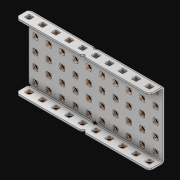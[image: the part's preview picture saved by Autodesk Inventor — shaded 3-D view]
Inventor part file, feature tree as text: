
AUTODESK INVENTOR PART (.ipt)
format: ipt  version: 2021 (Build 250183000, 183)  size: 3,073,024 bytes
history: native  units: in
note: dims shown in document units (in); Inventor stores cm internally (conversion verified against a paired STEP export)
features: extrude x71, other x70, sketch x4, thicken_offset x3, pattern_linear x3, imported_body x1
ambient origin geometry x8: Origin, YZ Plane, XZ Plane, XY Plane, X Axis, Y Axis, Z Axis, Center Point
bodies: Solid1 (feature_tree)
feature tree (152):
  thicken_offset  "Thicken1"
  thicken_offset  "Thicken2"
  thicken_offset  "Thicken3"
  pattern_linear  "Rectangular Pattern1"  Spacing1=0.001in  [1 undecoded]
  pattern_linear  "Rectangular Pattern2"  Spacing1=0.001in  [1 undecoded]
  pattern_linear  "Rectangular Pattern3"  Spacing1=0.182in  [1 undecoded]
  extrude  "Extrusion1"  Depth=0.063in TaperAngle=0.0deg
  sketch  "Sketch1"  dims[d0=0.001in]
  other  "Srf1"
  sketch  "Sketch2"  dims[d1=0.001in]
  other  "Srf2"
  sketch  "Sketch3"  dims[d2=0.001in]
  other  "Srf3"
  other  "Srf4"
  other  "Srf5"
  other  "Srf6"
  other  "Srf7"
  other  "Srf8"
  other  "Srf9"
  other  "Srf10"
  other  "Srf11"
  other  "Srf12"
  other  "Srf38"
  other  "Srf39"
  other  "Srf40"
  other  "Srf41"
  other  "Srf42"
  other  "Srf43"
  other  "Srf44"
  other  "Srf45"
  other  "Srf46"
  other  "Srf72"
  other  "Srf73"
  other  "Srf74"
  other  "Srf75"
  other  "Srf76"
  other  "Srf77"
  other  "Srf78"
  other  "Srf79"
  other  "Srf80"
  other  "Srf106"
  other  "Srf107"
  other  "Srf108"
  other  "Srf109"
  other  "Srf110"
  other  "Srf111"
  other  "Srf112"
  other  "Srf113"
  other  "Srf114"
  other  "Srf115"
  other  "Srf141"
  other  "Srf142"
  other  "Srf143"
  other  "Srf144"
  other  "Srf145"
  other  "Srf146"
  other  "Srf147"
  other  "Srf148"
  other  "Srf149"
  other  "Srf150"
  other  "Srf176"
  other  "Srf177"
  other  "Srf178"
  other  "Srf179"
  other  "Srf180"
  other  "Srf181"
  other  "Srf182"
  other  "Srf183"
  other  "Srf184"
  other  "Srf185"
  other  "Srf211"
  other  "Srf212"
  other  "Srf213"
  other  "Srf214"
  other  "Srf215"
  other  "Srf216"
  other  "Srf217"
  other  "Srf218"
  other  "Srf219"
  other  "Srf220"
  sketch  "Sketch4"  dims[d3=0.001in d4=0.001in d5=0.001in d6=0.182in d7=0.063in d8=0.0in d9=0.182in d10=0.063in d11=0.0in d12=0.182in d13=0.063in d14=0.0in d17=0.5in d18=3.937in d20=0.5in d21=3.937in d23=0.5in d24=1.9685in d26=0.5in d27=12.5in d28=0.0in]
  imported_body  "Imported1"
  extrude  "ExtrusionSrf1"  Depth=0.063in
  extrude  "ExtrusionSrf2"  Depth=0.063in TaperAngle=0.0deg
  extrude  "ExtrusionSrf3"  Depth=0.063in
  extrude  "ExtrusionSrf4"  Depth=0.063in TaperAngle=0.0deg
  extrude  "ExtrusionSrf5"  Depth=0.063in
  extrude  "ExtrusionSrf6"  Depth=0.063in
  extrude  "ExtrusionSrf7"  Depth=0.063in
  extrude  "ExtrusionSrf8"  Depth=0.063in
  extrude  "ExtrusionSrf9"  Depth=0.063in
  extrude  "ExtrusionSrf10"  Depth=0.063in
  extrude  "ExtrusionSrf11"  Depth=0.063in
  extrude  "ExtrusionSrf12"  TaperAngle=0.0deg  [1 undecoded]
  extrude  "ExtrusionSrf38"  [1 undecoded]
  extrude  "ExtrusionSrf39"  [1 undecoded]
  extrude  "ExtrusionSrf40"  [1 undecoded]
  extrude  "ExtrusionSrf41"  [1 undecoded]
  extrude  "ExtrusionSrf42"  [1 undecoded]
  extrude  "ExtrusionSrf43"  [1 undecoded]
  extrude  "ExtrusionSrf44"  [1 undecoded]
  extrude  "ExtrusionSrf45"  [1 undecoded]
  extrude  "ExtrusionSrf46"  [1 undecoded]
  extrude  "ExtrusionSrf72"  [1 undecoded]
  extrude  "ExtrusionSrf73"  [1 undecoded]
  extrude  "ExtrusionSrf74"  [1 undecoded]
  extrude  "ExtrusionSrf75"  [1 undecoded]
  extrude  "ExtrusionSrf76"  [1 undecoded]
  extrude  "ExtrusionSrf77"  [1 undecoded]
  extrude  "ExtrusionSrf78"  [1 undecoded]
  extrude  "ExtrusionSrf79"  [1 undecoded]
  extrude  "ExtrusionSrf80"  [1 undecoded]
  extrude  "ExtrusionSrf106"  [1 undecoded]
  extrude  "ExtrusionSrf107"  [1 undecoded]
  extrude  "ExtrusionSrf108"  [1 undecoded]
  extrude  "ExtrusionSrf109"  [1 undecoded]
  extrude  "ExtrusionSrf110"  [1 undecoded]
  extrude  "ExtrusionSrf111"  [1 undecoded]
  extrude  "ExtrusionSrf112"  [1 undecoded]
  extrude  "ExtrusionSrf113"  [1 undecoded]
  extrude  "ExtrusionSrf114"  [1 undecoded]
  extrude  "ExtrusionSrf115"  [1 undecoded]
  extrude  "ExtrusionSrf141"  [1 undecoded]
  extrude  "ExtrusionSrf142"  [1 undecoded]
  extrude  "ExtrusionSrf143"  [1 undecoded]
  extrude  "ExtrusionSrf144"  [1 undecoded]
  extrude  "ExtrusionSrf145"  [1 undecoded]
  extrude  "ExtrusionSrf146"  [1 undecoded]
  extrude  "ExtrusionSrf147"  [1 undecoded]
  extrude  "ExtrusionSrf148"  [1 undecoded]
  extrude  "ExtrusionSrf149"  [1 undecoded]
  extrude  "ExtrusionSrf150"  [1 undecoded]
  extrude  "ExtrusionSrf176"  [1 undecoded]
  extrude  "ExtrusionSrf177"  [1 undecoded]
  extrude  "ExtrusionSrf178"  [1 undecoded]
  extrude  "ExtrusionSrf179"  [1 undecoded]
  extrude  "ExtrusionSrf180"  [1 undecoded]
  extrude  "ExtrusionSrf181"  [1 undecoded]
  extrude  "ExtrusionSrf182"  [1 undecoded]
  extrude  "ExtrusionSrf183"  [1 undecoded]
  extrude  "ExtrusionSrf184"  [1 undecoded]
  extrude  "ExtrusionSrf185"  [1 undecoded]
  extrude  "ExtrusionSrf211"  [1 undecoded]
  extrude  "ExtrusionSrf212"  [1 undecoded]
  extrude  "ExtrusionSrf213"  [1 undecoded]
  extrude  "ExtrusionSrf214"  [1 undecoded]
  extrude  "ExtrusionSrf215"  [1 undecoded]
  extrude  "ExtrusionSrf216"  [1 undecoded]
  extrude  "ExtrusionSrf217"  [1 undecoded]
  extrude  "ExtrusionSrf218"  [1 undecoded]
  extrude  "ExtrusionSrf219"  [1 undecoded]
  extrude  "ExtrusionSrf220"  [1 undecoded]
note: 62 required parameter values undecoded (feature->parameter linkage not recoverable at this tier; creation-order binding heuristic only, values carry confidence <= 0.55)
